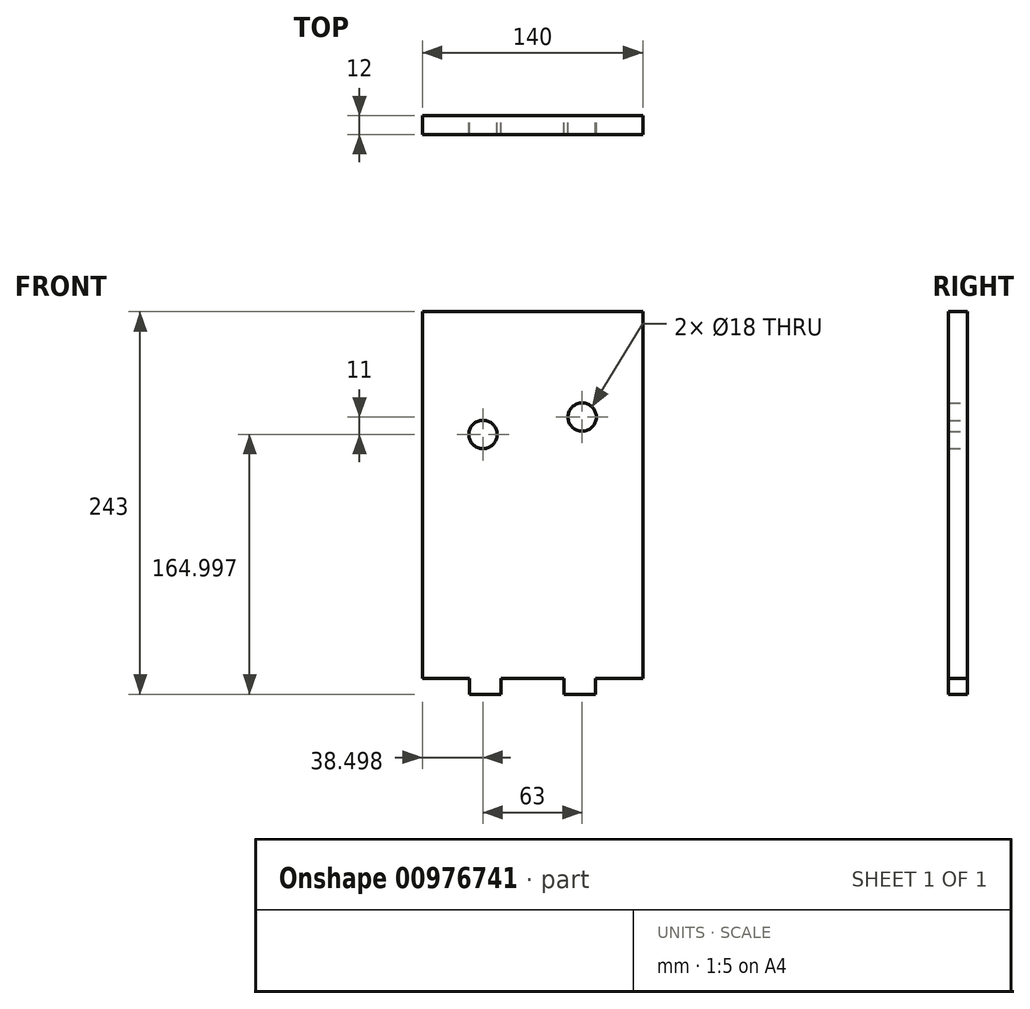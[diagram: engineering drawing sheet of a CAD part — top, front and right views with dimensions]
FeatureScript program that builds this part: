
annotation { "Feature Type Name" : "Feature", "Feature Type Description" : "" }
export const myFeature = defineFeature(function(context is Context, id is Id, definition is map)
    precondition{}
    {
        {
            var Q0;
            Q0=qCreatedBy(makeId("Front.planeOp"),FACE);
            var sketch = newSketch(context, id + "F0", { "sketchPlane" : qUnion([Q0])});
            skLineSegment(sketch, "E0.bottom", {"start": v(-297.63, 32.26) * mm, "end": v(-157.63, 32.26) * mm});
            skLineSegment(sketch, "E0.left", {"start": v(-297.63, 32.26) * mm, "end": v(-297.63, -200.74) * mm});
            skLineSegment(sketch, "E0.right", {"start": v(-157.63, 32.26) * mm, "end": v(-157.63, -200.74) * mm});
            skCircle(sketch, "E1", {"center": v(-259.13, -45.74) * mm, "radius": 9 * mm});
            skCircle(sketch, "E2", {"center": v(-196.13, -34.74) * mm, "radius": 9 * mm});
            skLineSegment(sketch, "E3", {"start": v(-297.63, -200.74) * mm, "end": v(-267.63, -200.74) * mm});
            skLineSegment(sketch, "E4", {"start": v(-267.63, -200.74) * mm, "end": v(-267.63, -210.74) * mm});
            skLineSegment(sketch, "E5", {"start": v(-267.63, -210.74) * mm, "end": v(-247.63, -210.74) * mm});
            skLineSegment(sketch, "E6", {"start": v(-247.63, -210.74) * mm, "end": v(-247.63, -200.74) * mm});
            skLineSegment(sketch, "E7", {"start": v(-247.63, -200.74) * mm, "end": v(-207.63, -200.74) * mm});
            skLineSegment(sketch, "E8", {"start": v(-207.63, -200.74) * mm, "end": v(-207.63, -210.74) * mm});
            skLineSegment(sketch, "E9", {"start": v(-207.63, -210.74) * mm, "end": v(-187.63, -210.74) * mm});
            skLineSegment(sketch, "E10", {"start": v(-187.63, -210.74) * mm, "end": v(-187.63, -200.74) * mm});
            skLineSegment(sketch, "E11", {"start": v(-187.63, -200.74) * mm, "end": v(-157.63, -200.74) * mm});
            skSolve(sketch);
        }
        {
            var Q0;
            Q0=makeQuery(id+"F0.imprint","IMPRINT",FACE,{"disambiguationData":[TD([[makeQuery(id+"F0.imprint","IMPRINT",EDGE,{"derivedFrom":sQuery(id+"F0.wireOp",EDGE,"E0.bottom")}),-1.0]])]});
            extrude(context, id + "F1", {"entities" : qUnion([Q0]), "depth" : 12 * mm, "offsetDistance" : 25 * mm});
        }
    });
